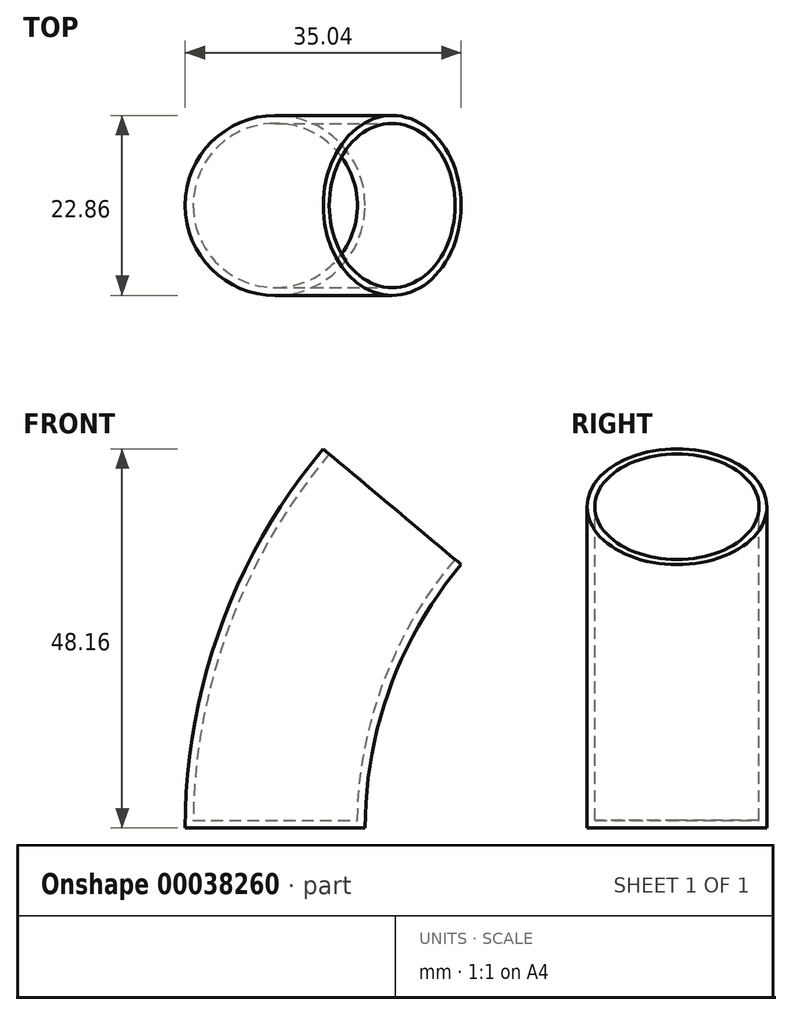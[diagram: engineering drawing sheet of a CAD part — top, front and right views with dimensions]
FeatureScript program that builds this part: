
annotation { "Feature Type Name" : "Feature", "Feature Type Description" : "" }
export const myFeature = defineFeature(function(context is Context, id is Id, definition is map)
    precondition{}
    {
        {
            var Q0;
            Q0=qCreatedBy(makeId("Top.planeOp"),FACE);
            var sketch = newSketch(context, id + "F0", { "sketchPlane" : qUnion([Q0])});
            skCircle(sketch, "E0", {"center": v(-63.5, 0) * mm, "radius": 11.43 * mm});
            skLineSegment(sketch, "E1", {"start": v(-63.5, 0) * mm, "end": v(0, 0) * mm, "construction": true});
            skLineSegment(sketch, "E2", {"start": v(0, 0) * mm, "end": v(0, 61.23) * mm, "construction": true});
            skSolve(sketch);
        }
        {
            var Q0;
            Q0 = qSketchRegion(id + "F0", true);
            var Q1;
            Q1=sQuery(id+"F0.wireOp",EDGE,"E2");
            revolve(context, id + "F1", {"entities" : qUnion([Q0]), "axis" : qUnion([Q1]), "revolveType" : RevolveType.FULL});
        }
        {
            var Q0;
            Q0=qCreatedBy(makeId("Front.planeOp"),FACE);
            var sketch = newSketch(context, id + "F2", { "sketchPlane" : qUnion([Q0])});
            skLineSegment(sketch, "E3", {"start": v(0, 0) * mm, "end": v(-77.83, 65.3) * mm});
            skLineSegment(sketch, "E4", {"start": v(0, 0) * mm, "end": v(-101.6, 0) * mm});
            skArc(sketch, "E5", {"start": v(-101.6, 0) * mm, "mid": v(95.47, -34.75) * mm, "end": v(-77.83, 65.3) * mm});
            skSolve(sketch);
        }
        {
            var Q0;
            Q0 = qSketchRegion(id + "F2", true);
            extrude(context, id + "F3", {"entities" : qUnion([Q0]), "operationType" : NewBodyOperationType.REMOVE, "endBound" : BoundingType.THROUGH_ALL, "oppositeDirection" : true, "depth" : 25.4 * mm, "hasSecondDirection" : true, "secondDirectionBound" : SecondDirectionBoundingType.THROUGH_ALL, "secondDirectionOppositeDirection" : false, "secondDirectionDepth" : 25.4 * mm});
        }
        {
            var Q0;
            Q0=makeQuery(id+"F3.boolean.opBoolean","COPY",FACE,{"derivedFrom":makeQuery(id+"F3.opExtrude","SWEPT_FACE",FACE,{"disambiguationData":[OSD([sQuery(id+"F2.wireOp",EDGE,"E3")])]})});
            shell(context, id + "F4", {"entities" : qUnion([Q0]), "thickness" : 1 * mm});
        }
    });
